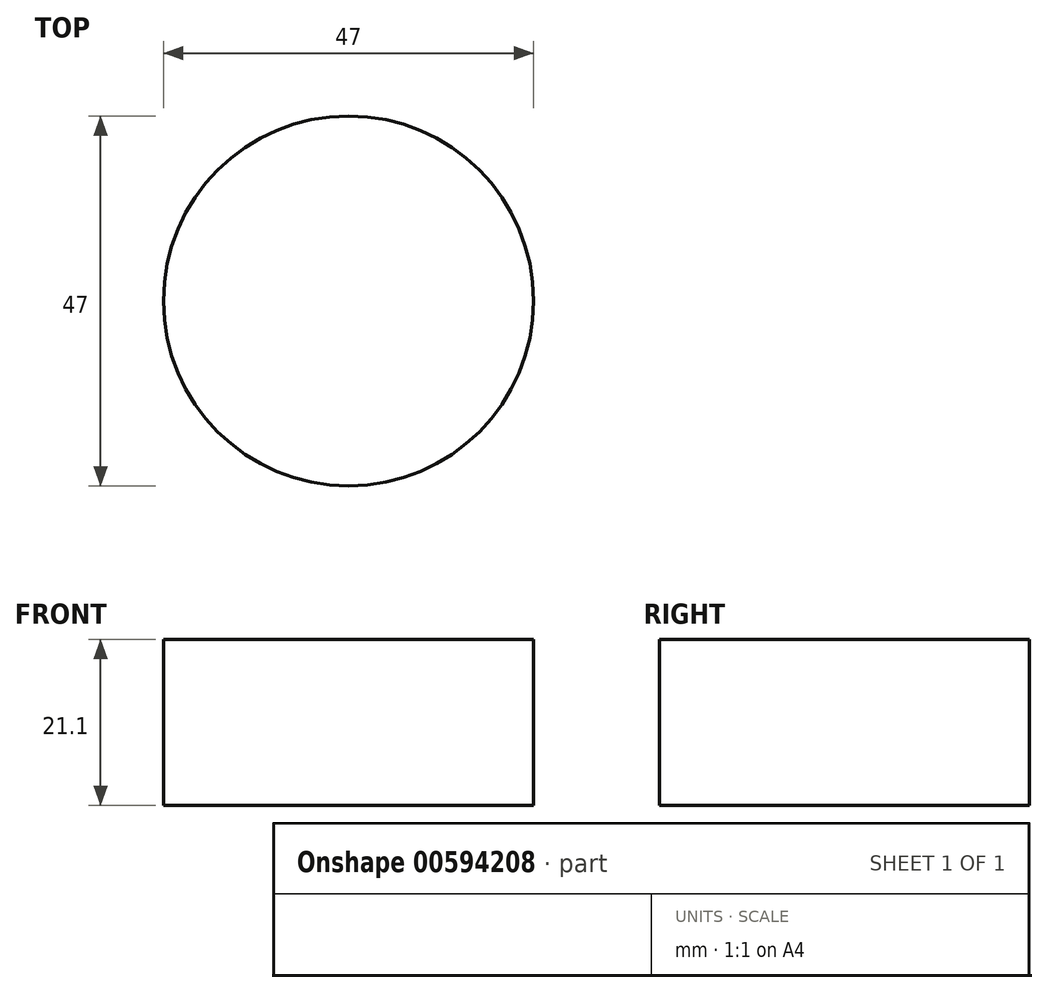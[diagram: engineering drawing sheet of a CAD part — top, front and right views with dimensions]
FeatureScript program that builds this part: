
annotation { "Feature Type Name" : "Feature", "Feature Type Description" : "" }
export const myFeature = defineFeature(function(context is Context, id is Id, definition is map)
    precondition{}
    {
        {
            var Q0;
            Q0=qCreatedBy(makeId("Front.planeOp"),FACE);
            var sketch = newSketch(context, id + "F0", { "sketchPlane" : qUnion([Q0])});
            skLineSegment(sketch, "E0", {"start": v(0, 0) * mm, "end": v(23.5, 0) * mm});
            skLineSegment(sketch, "E1", {"start": v(23.5, 0) * mm, "end": v(23.5, 21.1) * mm});
            skLineSegment(sketch, "E2", {"start": v(23.5, 21.1) * mm, "end": v(0, 21.1) * mm});
            skLineSegment(sketch, "E3", {"start": v(0, 21.1) * mm, "end": v(0, 0) * mm});
            skSolve(sketch);
        }
        {
            var Q0;
            Q0 = qSketchRegion(id + "F0", true);
            var Q1;
            Q1=sQuery(id+"F0.wireOp",EDGE,"E3");
            revolve(context, id + "F1", {"entities" : qUnion([Q0]), "axis" : qUnion([Q1]), "revolveType" : RevolveType.FULL});
        }
    });
